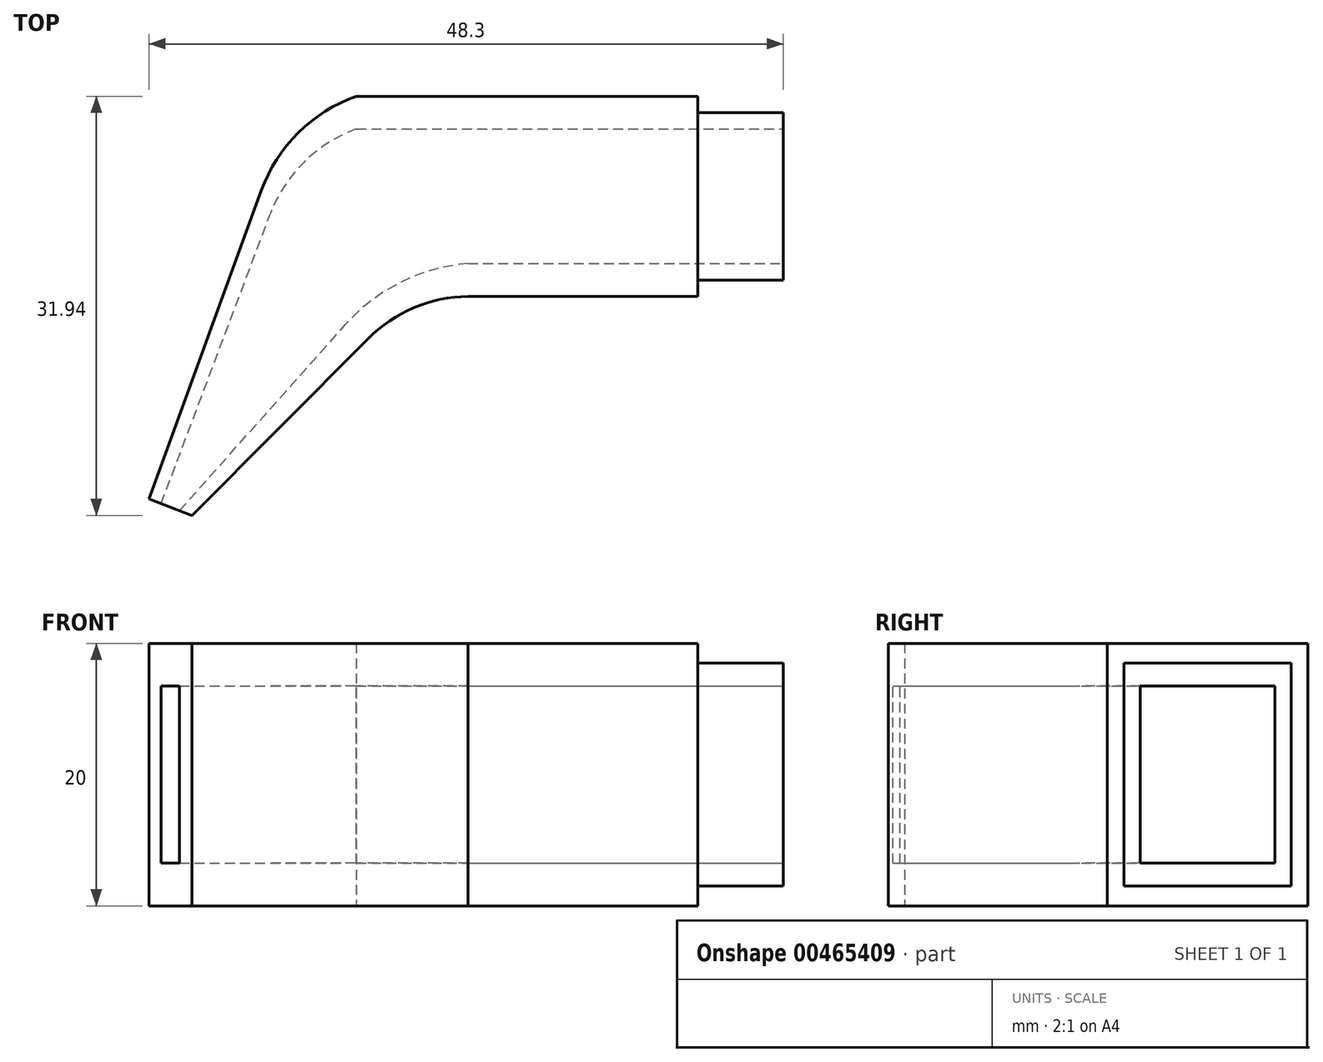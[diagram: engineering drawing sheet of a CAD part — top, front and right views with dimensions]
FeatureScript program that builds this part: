
annotation { "Feature Type Name" : "Feature", "Feature Type Description" : "" }
export const myFeature = defineFeature(function(context is Context, id is Id, definition is map)
    precondition{}
    {
        {
            var Q0;
            Q0=qCreatedBy(makeId("Top.planeOp"),FACE);
            var sketch = newSketch(context, id + "F0", { "sketchPlane" : qUnion([Q0])});
            skLineSegment(sketch, "E0", {"start": v(28.76, 0) * mm, "end": v(28.76, 12.75) * mm});
            skLineSegment(sketch, "E1", {"start": v(28.76, 12.75) * mm, "end": v(11.26, 12.75) * mm});
            skLineSegment(sketch, "E2", {"start": v(11.26, 12.75) * mm, "end": v(11.26, 0) * mm});
            skLineSegment(sketch, "E3", {"start": v(11.26, 0) * mm, "end": v(28.76, 0) * mm});
            skLineSegment(sketch, "E4", {"start": v(-9.77, -17.94) * mm, "end": v(3.64, -4.48) * mm});
            skArc(sketch, "E5", {"start": v(3.64, -4.48) * mm, "mid": v(7.14, -2.12) * mm, "end": v(11.26, -1.25) * mm});
            skLineSegment(sketch, "E6", {"start": v(11.26, -1.25) * mm, "end": v(11.26, 0) * mm});
            skLineSegment(sketch, "E7", {"start": v(11.26, 14) * mm, "end": v(2.76, 14) * mm});
            skLineSegment(sketch, "E8", {"start": v(-13.04, -16.69) * mm, "end": v(-4.48, 6.8) * mm});
            skArc(sketch, "E9", {"start": v(-4.48, 6.8) * mm, "mid": v(-1.66, 11.21) * mm, "end": v(2.76, 14) * mm});
            skLineSegment(sketch, "E10", {"start": v(11.26, 12.75) * mm, "end": v(11.26, 14) * mm});
            skLineSegment(sketch, "E11", {"start": v(11.26, 1.25) * mm, "end": v(28.76, 1.25) * mm});
            skLineSegment(sketch, "E12", {"start": v(11.26, 11.5) * mm, "end": v(2.76, 11.5) * mm});
            skLineSegment(sketch, "E13", {"start": v(-12.1, -17.05) * mm, "end": v(-3.8, 5.03) * mm});
            skArc(sketch, "E14", {"start": v(-3.8, 5.03) * mm, "mid": v(-1.22, 8.98) * mm, "end": v(2.76, 11.5) * mm});
            skLineSegment(sketch, "E15", {"start": v(11.26, 11.5) * mm, "end": v(28.76, 11.5) * mm});
            skLineSegment(sketch, "E16.bottom", {"start": v(28.76, 12.75) * mm, "end": v(35.26, 12.75) * mm});
            skLineSegment(sketch, "E16.top", {"start": v(28.76, 1.25) * mm, "end": v(35.26, 1.25) * mm});
            skLineSegment(sketch, "E16.left", {"start": v(28.76, 12.75) * mm, "end": v(28.76, 1.25) * mm});
            skLineSegment(sketch, "E16.right", {"start": v(35.26, 12.75) * mm, "end": v(35.26, 1.25) * mm});
            skLineSegment(sketch, "E17", {"start": v(28.76, 11.5) * mm, "end": v(35.26, 11.5) * mm});
            skLineSegment(sketch, "E18", {"start": v(28.76, 0) * mm, "end": v(35.26, 0) * mm});
            skLineSegment(sketch, "E19", {"start": v(35.26, 0) * mm, "end": v(35.26, 1.25) * mm});
            skLineSegment(sketch, "E20", {"start": v(11.26, 14) * mm, "end": v(28.76, 14) * mm});
            skLineSegment(sketch, "E21", {"start": v(28.76, 14) * mm, "end": v(28.76, 12.75) * mm});
            skLineSegment(sketch, "E22", {"start": v(11.26, -1.25) * mm, "end": v(28.76, -1.25) * mm});
            skLineSegment(sketch, "E23", {"start": v(28.76, -1.25) * mm, "end": v(28.76, 0) * mm});
            skLineSegment(sketch, "E24", {"start": v(-10.7, -17.58) * mm, "end": v(1.93, -3.4) * mm});
            skArc(sketch, "E25", {"start": v(1.93, -3.4) * mm, "mid": v(6.15, -0.17) * mm, "end": v(11.26, 1.25) * mm});
            skLineSegment(sketch, "E26", {"start": v(-9.77, -17.94) * mm, "end": v(-13.04, -16.69) * mm});
            skSolve(sketch);
        }
        {
            var Q0;
            Q0=makeQuery(id+"F0.imprint","IMPRINT",FACE,{"disambiguationData":[TD([[makeQuery(id+"F0.imprint","IMPRINT",EDGE,{"derivedFrom":sQuery(id+"F0.wireOp",EDGE,"0i2drSoP-zeYy-nr1m-dSU6-w7wf3uXWtFC1")}),-1.0]])]});
            var Q1;
            {var subQ1=sQuery(id+"F0.wireOp",EDGE,"0i2drSoP-zeYy-nr1m-dSU6-w7wf3uXWtFC1");Q1=makeQuery(id+"F0.imprint","IMPRINT",FACE,{"disambiguationData":[TD([[makeQuery(id+"F0.imprint","IMPRINT",EDGE,{"derivedFrom":subQ1}),1.0]])]});}
            var Q2;
            {var subQ1=sQuery(id+"F0.wireOp",EDGE,"VvqijoO1-KL1r-lRlq-ZBw7-lMvZobiEQYsp");Q2=makeQuery(id+"F0.imprint","IMPRINT",FACE,{"disambiguationData":[TD([[makeQuery(id+"F0.imprint","IMPRINT",EDGE,{"derivedFrom":subQ1}),1.0]])]});}
            var Q3;
            Q3=makeQuery(id+"F0.imprint","IMPRINT",FACE,{"disambiguationData":[TD([[makeQuery(id+"F0.imprint","IMPRINT",EDGE,{"derivedFrom":sQuery(id+"F0.wireOp",EDGE,"VvqijoO1-KL1r-lRlq-ZBw7-lMvZobiEQYsp")}),-1.0]])]});
            var Q4;
            Q4=makeQuery(id+"F0.imprint","IMPRINT",FACE,{"disambiguationData":[TD([[makeQuery(id+"F0.imprint","IMPRINT",EDGE,{"derivedFrom":sQuery(id+"F0.wireOp",EDGE,"E1")}),-1.0]])]});
            var Q5;
            {var subQ0=sQuery(id+"F0.wireOp",EDGE,"E1");Q5=makeQuery(id+"F0.imprint","IMPRINT",FACE,{"disambiguationData":[TD([[makeQuery(id+"F0.imprint","IMPRINT",EDGE,{"derivedFrom":subQ0}),1.0]])]});}
            var Q6;
            Q6=makeQuery(id+"F0.imprint","IMPRINT",FACE,{"disambiguationData":[TD([[makeQuery(id+"F0.imprint","IMPRINT",EDGE,{"derivedFrom":sQuery(id+"F0.wireOp",EDGE,"E0")}),1.0]])]});
            var Q7;
            Q7=makeQuery(id+"F0.imprint","IMPRINT",FACE,{"disambiguationData":[TD([[makeQuery(id+"F0.imprint","IMPRINT",EDGE,{"derivedFrom":sQuery(id+"F0.wireOp",EDGE,"E3")}),-1.0]])]});
            var Q8;
            {var subQ1=sQuery(id+"F0.wireOp",EDGE,"43087bad-841d-4768-8d66-cc5accd6c26b");Q8=makeQuery(id+"F0.imprint","IMPRINT",FACE,{"disambiguationData":[TD([[makeQuery(id+"F0.imprint","IMPRINT",EDGE,{"derivedFrom":subQ1}),1.0]])]});}
            var Q9;
            Q9=makeQuery(id+"F0.imprint","IMPRINT",FACE,{"disambiguationData":[TD([[makeQuery(id+"F0.imprint","IMPRINT",EDGE,{"derivedFrom":sQuery(id+"F0.wireOp",EDGE,"E4")}),1.0]])]});
            var Q10;
            Q10=makeQuery(id+"F0.imprint","IMPRINT",FACE,{"disambiguationData":[TD([[makeQuery(id+"F0.imprint","IMPRINT",EDGE,{"derivedFrom":sQuery(id+"F0.wireOp",EDGE,"E7")}),1.0]])]});
            extrude(context, id + "F1", {"entities" : qUnion([Q0, Q1, Q2, Q3, Q4, Q5, Q6, Q7, Q8, Q9, Q10]), "flatOperationType" : FlatOperationType.REMOVE, "endBound" : BoundingType.SYMMETRIC, "offsetDistance" : 25 * mm, "depth" : 20 * mm, "domain" : OperationDomain.MODEL});
        }
        {
            var Q0;
            {var subQ1=sQuery(id+"F0.wireOp",EDGE,"6c897192-de31-4fd1-aa90-0388c48c0e31");Q0=makeQuery(id+"F0.imprint","IMPRINT",FACE,{"disambiguationData":[TD([[makeQuery(id+"F0.imprint","IMPRINT",EDGE,{"derivedFrom":subQ1}),1.0]])]});}
            var Q1;
            {var subQ0=sQuery(id+"F0.wireOp",EDGE,"E11");Q1=makeQuery(id+"F0.imprint","IMPRINT",FACE,{"disambiguationData":[TD([[makeQuery(id+"F0.imprint","IMPRINT",EDGE,{"derivedFrom":subQ0}),1.0]])]});}
            var Q2;
            {var subQ2=sQuery(id+"F0.wireOp",EDGE,"E12");Q2=makeQuery(id+"F0.imprint","IMPRINT",FACE,{"disambiguationData":[TD([[makeQuery(id+"F0.imprint","IMPRINT",EDGE,{"derivedFrom":subQ2}),1.0]])]});}
            extrude(context, id + "F2", {"entities" : qUnion([Q0, Q1, Q2]), "operationType" : NewBodyOperationType.ADD, "flatOperationType" : FlatOperationType.REMOVE, "endBound" : BoundingType.SYMMETRIC, "depth" : 20 * mm, "offsetDistance" : 25 * mm, "domain" : OperationDomain.MODEL});
        }
        {
            var Q0;
            {var subQ0=sQuery(id+"F0.wireOp",EDGE,"E16.bottom");Q0=makeQuery(id+"F0.imprint","IMPRINT",FACE,{"disambiguationData":[TD([[makeQuery(id+"F0.imprint","IMPRINT",EDGE,{"derivedFrom":subQ0}),-1.0]])]});}
            var Q1;
            {var subQ0=sQuery(id+"F0.wireOp",EDGE,"E16.top");Q1=makeQuery(id+"F0.imprint","IMPRINT",FACE,{"disambiguationData":[TD([[makeQuery(id+"F0.imprint","IMPRINT",EDGE,{"derivedFrom":subQ0}),1.0]])]});}
            var Q2;
            Q2=makeQuery(id+"F0.imprint","IMPRINT",FACE,{"disambiguationData":[TD([[makeQuery(id+"F0.imprint","IMPRINT",EDGE,{"derivedFrom":sQuery(id+"F0.wireOp",EDGE,"E0")}),-1.0]])]});
            extrude(context, id + "F3", {"entities" : qUnion([Q0, Q1, Q2]), "operationType" : NewBodyOperationType.ADD, "flatOperationType" : FlatOperationType.REMOVE, "endBound" : BoundingType.SYMMETRIC, "depth" : 17 * mm, "offsetDistance" : 25 * mm, "domain" : OperationDomain.MODEL});
        }
        {
            var Q0;
            {var subQ1=sQuery(id+"F0.wireOp",EDGE,"6c897192-de31-4fd1-aa90-0388c48c0e31");Q0=makeQuery(id+"F0.imprint","IMPRINT",FACE,{"disambiguationData":[TD([[makeQuery(id+"F0.imprint","IMPRINT",EDGE,{"derivedFrom":subQ1}),1.0]])]});}
            var Q1;
            {var subQ0=sQuery(id+"F0.wireOp",EDGE,"E11");Q1=makeQuery(id+"F0.imprint","IMPRINT",FACE,{"disambiguationData":[TD([[makeQuery(id+"F0.imprint","IMPRINT",EDGE,{"derivedFrom":subQ0}),1.0]])]});}
            var Q2;
            {var subQ2=sQuery(id+"F0.wireOp",EDGE,"E12");Q2=makeQuery(id+"F0.imprint","IMPRINT",FACE,{"disambiguationData":[TD([[makeQuery(id+"F0.imprint","IMPRINT",EDGE,{"derivedFrom":subQ2}),1.0]])]});}
            extrude(context, id + "F4", {"entities" : qUnion([Q0, Q1, Q2]), "operationType" : NewBodyOperationType.REMOVE, "flatOperationType" : FlatOperationType.REMOVE, "endBound" : BoundingType.SYMMETRIC, "oppositeDirection" : true, "depth" : 13.5 * mm, "offsetDistance" : 25 * mm, "domain" : OperationDomain.MODEL});
        }
        {
            var Q0;
            {var subQ0=sQuery(id+"F0.wireOp",EDGE,"E16.top");Q0=makeQuery(id+"F0.imprint","IMPRINT",FACE,{"disambiguationData":[TD([[makeQuery(id+"F0.imprint","IMPRINT",EDGE,{"derivedFrom":subQ0}),1.0]])]});}
            extrude(context, id + "F5", {"entities" : qUnion([Q0]), "operationType" : NewBodyOperationType.REMOVE, "endBound" : BoundingType.SYMMETRIC, "oppositeDirection" : true, "depth" : 13.5 * mm, "offsetDistance" : 25 * mm});
        }
    });
